# Revit family: Podajnik_reczników_w_roli POP
name_source: partatom
category: Furniture
units: mm (PartAtom-declared; Revit-internal decimal feet)

## family parameters
Always vertical = Yes
Cut with Voids When Loaded = No
Host = Wall
Room Calculation Point = No
Shared = No

## types (1)
- Type 1
    Color / Kolor = White-Grey / Biały-Szary
    Depth / Glebokosc = 210 mm  [stored 0.688976 ft]
    Description = Podajnik ręczników w roli POP to wykonany z mocnego, białego plastiku ABS naścienny pojemnik, posiadający atest PZH. Gwarantuje on bezpieczeństwo i higienę, dlatego jest idealny do szkół, gabinetów lekarskich czy lokali gastronomicznych. Umożliwia dozowanie ręczników bez kontaktu z obudową. To łatwy w montażu, obsłudze i utrzymywaniu czystości dozownik ręczników papierowych.
    Height / Wysokosc = 310 mm  [stored 1.01706 ft]
    Manufacturer = FANECO.com
    Manufacturer code / Kod producenta = 5901764290148
    Material finish / Wykonczenie = Plastic ABS
    Model = POP
    Product code / Kod produktu = P22PGWG
    Type Comments = Podajnik ręczników w roli POP
    URL = https://faneco.com
    Weight / Waga = 0.95 kg
    Width / Szerokosc = 220 mm  [stored 0.721785 ft]

note: [stored X ft] marks values corroborated as IEEE doubles in the binary element streams (Revit-internal decimal feet)

## geometry (parser evidence)
native form markers: Blend x2, Sweep x9
no freeform markers — native parametric forms only
